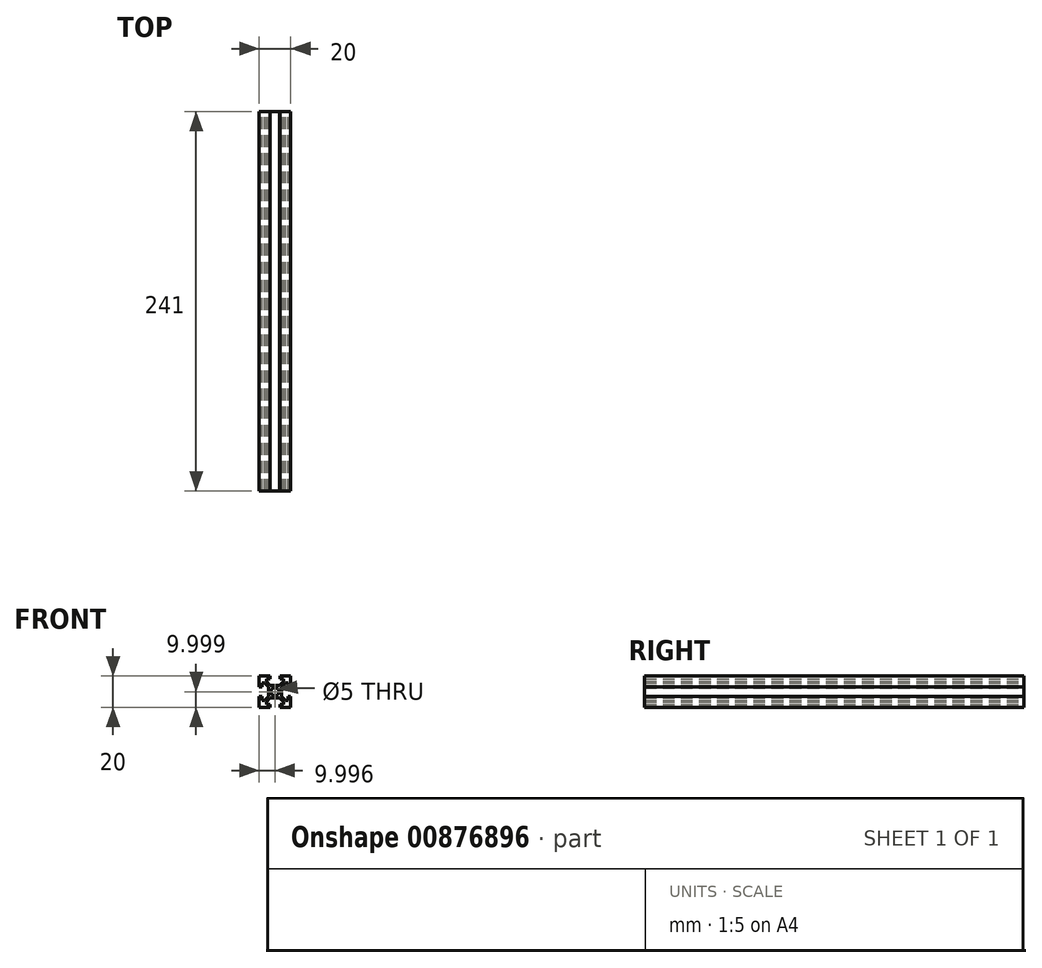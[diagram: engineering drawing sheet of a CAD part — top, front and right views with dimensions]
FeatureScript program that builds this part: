
annotation { "Feature Type Name" : "Feature", "Feature Type Description" : "" }
export const myFeature = defineFeature(function(context is Context, id is Id, definition is map)
    precondition{}
    {
        {
            var Q0;
            Q0=qCreatedBy(makeId("Front.planeOp"),FACE);
            var sketch = newSketch(context, id + "F0", { "sketchPlane" : qUnion([Q0])});
            skLineSegment(sketch, "E0.bottom", {"start": v(30.52, 43.29) * mm, "end": v(50.52, 43.29) * mm});
            skLineSegment(sketch, "E0.top", {"start": v(30.52, 23.29) * mm, "end": v(50.52, 23.29) * mm});
            skLineSegment(sketch, "E0.left", {"start": v(30.52, 43.29) * mm, "end": v(30.52, 23.29) * mm});
            skLineSegment(sketch, "E0.right", {"start": v(50.52, 43.29) * mm, "end": v(50.52, 23.29) * mm});
            skPoint(sketch, "E0.middle", {"position": v(40.52, 33.29) * mm});
            skLineSegment(sketch, "E1", {"start": v(48.72, 36.39) * mm, "end": v(50.52, 36.39) * mm});
            skLineSegment(sketch, "E2.MirrorCS", {"start": v(48.72, 30.19) * mm, "end": v(50.52, 30.19) * mm});
            skLineSegment(sketch, "E3", {"start": v(48.72, 36.39) * mm, "end": v(48.72, 38.79) * mm});
            skLineSegment(sketch, "E4.MirrorCS", {"start": v(48.72, 30.19) * mm, "end": v(48.72, 27.79) * mm});
            skLineSegment(sketch, "E5", {"start": v(48.72, 38.79) * mm, "end": v(47.12, 38.79) * mm});
            skLineSegment(sketch, "E6.MirrorCS", {"start": v(48.72, 27.79) * mm, "end": v(47.12, 27.79) * mm});
            skCircle(sketch, "E7", {"center": v(40.52, 33.29) * mm, "radius": 2.5 * mm});
            skLineSegment(sketch, "E8", {"start": v(44.62, 36.29) * mm, "end": v(44.62, 30.29) * mm});
            skLineSegment(sketch, "E9", {"start": v(44.62, 36.29) * mm, "end": v(47.12, 38.79) * mm});
            skLineSegment(sketch, "E10.MirrorCS", {"start": v(44.62, 30.29) * mm, "end": v(47.12, 27.79) * mm});
            skLineSegment(sketch, "E11.MirrorCS", {"start": v(32.32, 36.39) * mm, "end": v(30.52, 36.39) * mm});
            skLineSegment(sketch, "E12.MirrorCS", {"start": v(32.32, 36.39) * mm, "end": v(32.32, 38.79) * mm});
            skLineSegment(sketch, "E13.MirrorCS", {"start": v(32.32, 38.79) * mm, "end": v(33.92, 38.79) * mm});
            skLineSegment(sketch, "E14.MirrorCS", {"start": v(36.42, 36.29) * mm, "end": v(33.92, 38.79) * mm});
            skLineSegment(sketch, "E15.MirrorCS", {"start": v(36.42, 36.29) * mm, "end": v(36.42, 30.29) * mm});
            skLineSegment(sketch, "E16.MirrorCS", {"start": v(36.42, 30.29) * mm, "end": v(33.92, 27.79) * mm});
            skLineSegment(sketch, "E17.MirrorCS", {"start": v(32.32, 27.79) * mm, "end": v(33.92, 27.79) * mm});
            skLineSegment(sketch, "E18.MirrorCS", {"start": v(32.32, 30.19) * mm, "end": v(32.32, 27.79) * mm});
            skLineSegment(sketch, "E19.MirrorCS", {"start": v(32.32, 30.19) * mm, "end": v(30.52, 30.19) * mm});
            skLineSegment(sketch, "E20", {"start": v(37.42, 43.29) * mm, "end": v(37.42, 41.49) * mm});
            skLineSegment(sketch, "E21", {"start": v(37.42, 41.49) * mm, "end": v(35.02, 41.49) * mm});
            skLineSegment(sketch, "E22", {"start": v(35.02, 41.49) * mm, "end": v(35.02, 39.89) * mm});
            skLineSegment(sketch, "E23", {"start": v(37.52, 37.39) * mm, "end": v(40.52, 37.39) * mm});
            skLineSegment(sketch, "E24.MirrorCS", {"start": v(43.62, 43.29) * mm, "end": v(43.62, 41.49) * mm});
            skLineSegment(sketch, "E25.MirrorCS", {"start": v(43.62, 41.49) * mm, "end": v(46.02, 41.49) * mm});
            skLineSegment(sketch, "E26.MirrorCS", {"start": v(46.02, 41.49) * mm, "end": v(46.02, 39.89) * mm});
            skLineSegment(sketch, "E27.MirrorCS", {"start": v(43.52, 37.39) * mm, "end": v(40.52, 37.39) * mm});
            skLineSegment(sketch, "E28", {"start": v(46.02, 39.89) * mm, "end": v(43.52, 37.39) * mm});
            skLineSegment(sketch, "E29", {"start": v(35.02, 39.89) * mm, "end": v(37.52, 37.39) * mm});
            skLineSegment(sketch, "E30.MirrorCS", {"start": v(37.42, 23.29) * mm, "end": v(37.42, 25.09) * mm});
            skLineSegment(sketch, "E31.MirrorCS", {"start": v(37.42, 25.09) * mm, "end": v(35.02, 25.09) * mm});
            skLineSegment(sketch, "E32.MirrorCS", {"start": v(35.02, 25.09) * mm, "end": v(35.02, 26.69) * mm});
            skLineSegment(sketch, "E33.MirrorCS", {"start": v(35.02, 26.69) * mm, "end": v(37.52, 29.19) * mm});
            skLineSegment(sketch, "E34.MirrorCS", {"start": v(43.62, 23.29) * mm, "end": v(43.62, 25.09) * mm});
            skLineSegment(sketch, "E35.MirrorCS", {"start": v(43.62, 25.09) * mm, "end": v(46.02, 25.09) * mm});
            skLineSegment(sketch, "E36.MirrorCS", {"start": v(46.02, 25.09) * mm, "end": v(46.02, 26.69) * mm});
            skLineSegment(sketch, "E37.MirrorCS", {"start": v(46.02, 26.69) * mm, "end": v(43.52, 29.19) * mm});
            skLineSegment(sketch, "E38.MirrorCS", {"start": v(43.52, 29.19) * mm, "end": v(40.52, 29.19) * mm});
            skLineSegment(sketch, "E39.MirrorCS", {"start": v(37.52, 29.19) * mm, "end": v(40.52, 29.19) * mm});
            skSolve(sketch);
        }
        {
            var Q0;
            {var subQ5=sQuery(id+"F0.wireOp",EDGE,"E1");Q0=makeQuery(id+"F0.imprint","IMPRINT",FACE,{"disambiguationData":[TD([[makeQuery(id+"F0.imprint","IMPRINT",EDGE,{"derivedFrom":subQ5}),1.0]])]});}
            extrude(context, id + "F1", {"entities" : qUnion([Q0]), "depth" : 241 * mm, "offsetDistance" : 25 * mm});
        }
    });
